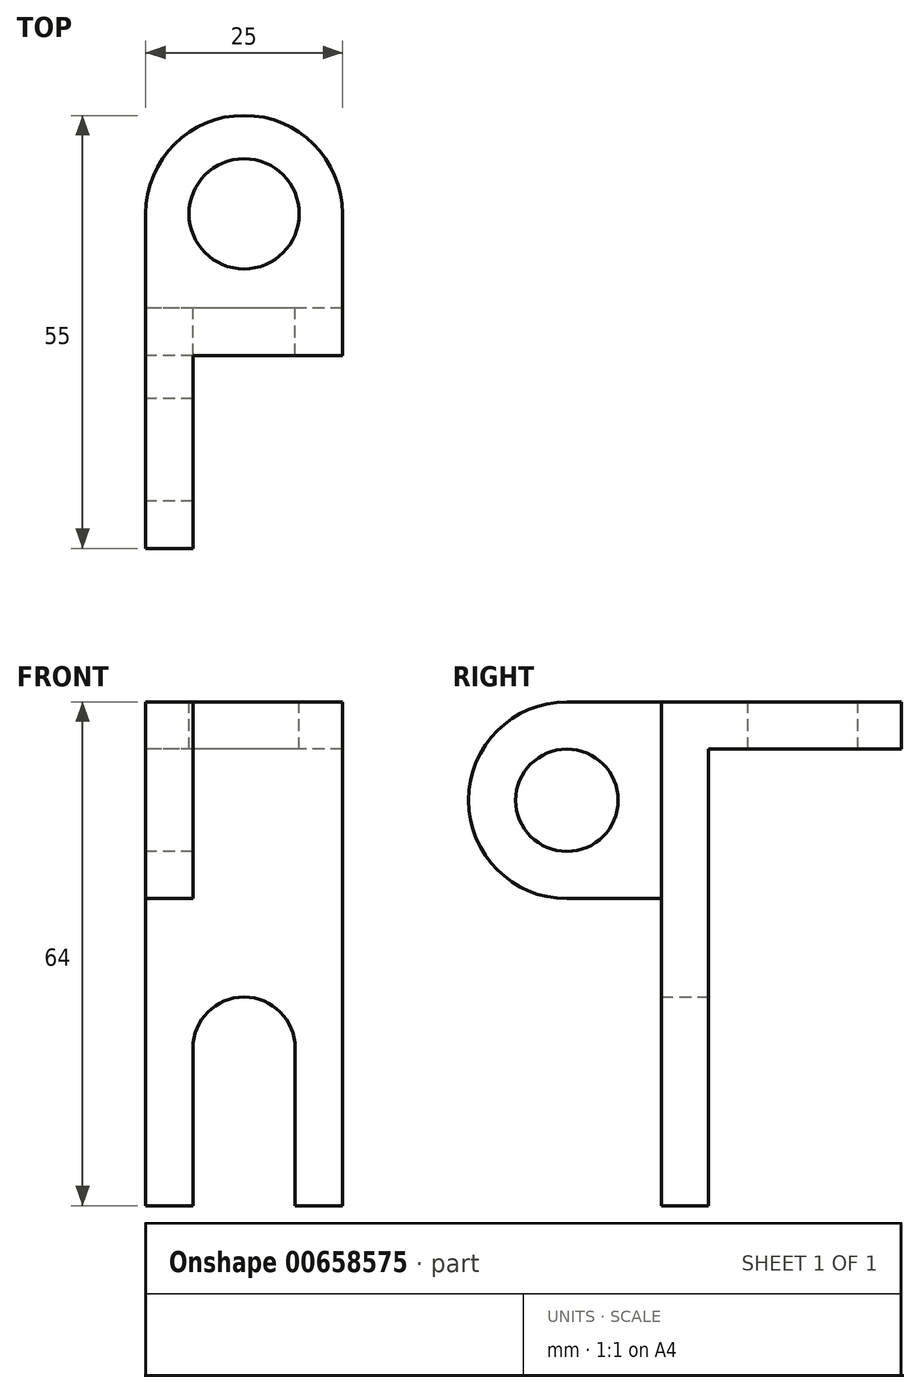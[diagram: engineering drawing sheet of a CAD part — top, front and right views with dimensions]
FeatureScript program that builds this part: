
annotation { "Feature Type Name" : "Feature", "Feature Type Description" : "" }
export const myFeature = defineFeature(function(context is Context, id is Id, definition is map)
    precondition{}
    {
        {
            var Q0;
            Q0=qCreatedBy(makeId("Front.planeOp"),FACE);
            var sketch = newSketch(context, id + "F0", { "sketchPlane" : qUnion([Q0])});
            skLineSegment(sketch, "E0.bottom", {"start": v(12.5, -32) * mm, "end": v(-12.5, -32) * mm});
            skLineSegment(sketch, "E0.top", {"start": v(12.5, 32) * mm, "end": v(-12.5, 32) * mm});
            skLineSegment(sketch, "E0.left", {"start": v(12.5, -32) * mm, "end": v(12.5, 32) * mm});
            skLineSegment(sketch, "E0.right", {"start": v(-12.5, -32) * mm, "end": v(-12.5, 32) * mm});
            skPoint(sketch, "E0.middle", {"position": v(0, 0) * mm});
            skLineSegment(sketch, "E1.bottom", {"start": v(-6.5, -32) * mm, "end": v(6.5, -32) * mm});
            skLineSegment(sketch, "E1.top", {"start": v(-6.5, -12) * mm, "end": v(6.5, -12) * mm});
            skLineSegment(sketch, "E1.left", {"start": v(-6.5, -32) * mm, "end": v(-6.5, -12) * mm});
            skLineSegment(sketch, "E1.right", {"start": v(6.5, -32) * mm, "end": v(6.5, -12) * mm});
            skPoint(sketch, "E1.middle", {"position": v(0, -22) * mm});
            skCircle(sketch, "E2", {"center": v(0, -12) * mm, "radius": 6.5 * mm});
            skSolve(sketch);
        }
        {
            var Q0;
            Q0=makeQuery(id+"F0.imprint","IMPRINT",FACE,{"disambiguationData":[TD([[makeQuery(id+"F0.imprint","IMPRINT",EDGE,{"derivedFrom":sQuery(id+"F0.wireOp",EDGE,"E0.bottom")}),-1.0]])]});
            extrude(context, id + "F1", {"entities" : qUnion([Q0]), "depth" : 6 * mm, "offsetDistance" : 25 * mm});
        }
        {
            var Q0;
            Q0=makeQuery(id+"F1.opExtrude","SWEPT_FACE",FACE,{"disambiguationData":[OSD([sQuery(id+"F0.wireOp",EDGE,"E0.top")])]});
            var sketch = newSketch(context, id + "F2", { "sketchPlane" : qUnion([Q0])});
            skLineSegment(sketch, "E3.bottom", {"start": v(12.5, -6) * mm, "end": v(-12.5, -6) * mm});
            skLineSegment(sketch, "E3.top", {"start": v(12.5, 12) * mm, "end": v(7, 12) * mm, "construction": true});
            skLineSegment(sketch, "E3.left", {"start": v(12.5, -6) * mm, "end": v(12.5, 12) * mm});
            skLineSegment(sketch, "E3.right", {"start": v(-12.5, -6) * mm, "end": v(-12.5, 12) * mm});
            skArc(sketch, "E4", {"start": v(12.5, 12) * mm, "mid": v(0, 24.5) * mm, "end": v(-12.5, 12) * mm});
            skCircle(sketch, "E5", {"center": v(0, 12) * mm, "radius": 7 * mm});
            skLineSegment(sketch, "E6.trimOffspring", {"start": v(-7, 12) * mm, "end": v(-12.5, 12) * mm, "construction": true});
            skSolve(sketch);
        }
        {
            var Q0;
            {var subQ0=sQuery(id+"F2.wireOp",EDGE,"E4");Q0=makeQuery(id+"F2.imprint","IMPRINT",FACE,{"disambiguationData":[TD([[makeQuery(id+"F2.imprint","IMPRINT",EDGE,{"derivedFrom":subQ0}),1.0]])]});}
            extrude(context, id + "F3", {"entities" : qUnion([Q0]), "operationType" : NewBodyOperationType.ADD, "oppositeDirection" : true, "depth" : 6 * mm, "offsetDistance" : 25 * mm});
        }
        {
            var Q0;
            Q0=makeQuery(id+"F3.boolean.opBoolean","MERGE",FACE,{"derivedFrom":[makeQuery(id+"F1.opExtrude","SWEPT_FACE",FACE,{"disambiguationData":[OSD([sQuery(id+"F0.wireOp",EDGE,"E0.right")])]}),makeQuery(id+"F3.opExtrude","SWEPT_FACE",FACE,{"disambiguationData":[OSD([sQuery(id+"F2.wireOp",EDGE,"E3.right")])]})]});
            var sketch = newSketch(context, id + "F4", { "sketchPlane" : qUnion([Q0])});
            skLineSegment(sketch, "E7.bottom", {"start": v(0, 32) * mm, "end": v(18, 32) * mm});
            skLineSegment(sketch, "E7.top", {"start": v(0, 7) * mm, "end": v(18, 7) * mm});
            skLineSegment(sketch, "E7.left", {"start": v(0, 32) * mm, "end": v(0, 7) * mm});
            skLineSegment(sketch, "E7.right", {"start": v(18, 32) * mm, "end": v(18, 7) * mm});
            skArc(sketch, "E8", {"start": v(18, 7) * mm, "mid": v(30.5, 19.5) * mm, "end": v(18, 32) * mm});
            skSolve(sketch);
        }
        {
            var Q0;
            {var subQ4=sQuery(id+"F4.wireOp",EDGE,"E7.right");Q0=makeQuery(id+"F4.imprint","IMPRINT",FACE,{"disambiguationData":[TD([[makeQuery(id+"F4.imprint","IMPRINT",EDGE,{"derivedFrom":subQ4}),-1.0]])]});}
            var Q1;
            Q1=makeQuery(id+"F4.imprint","IMPRINT",FACE,{"disambiguationData":[TD([[makeQuery(id+"F4.imprint","IMPRINT",EDGE,{"derivedFrom":sQuery(id+"F4.wireOp",EDGE,"E7.right")}),1.0]])]});
            extrude(context, id + "F5", {"entities" : qUnion([Q0, Q1]), "operationType" : NewBodyOperationType.ADD, "oppositeDirection" : true, "depth" : 6 * mm, "offsetDistance" : 25 * mm});
        }
        {
            var Q0;
            Q0=sQuery(id+"F4.wireOp",VERTEX,"E8.center");
            var Q1;
            Q1=makeQuery(id+"F1.opExtrude","SWEPT_BODY",BODY,{"disambiguationData":[OSD([sQuery(id+"F0.wireOp",EDGE,"E0.bottom"),sQuery(id+"F0.wireOp",EDGE,"E0.top"),sQuery(id+"F0.wireOp",EDGE,"E0.left"),sQuery(id+"F0.wireOp",EDGE,"E0.right"),sQuery(id+"F0.wireOp",EDGE,"E1.left"),sQuery(id+"F0.wireOp",EDGE,"E1.right"),sQuery(id+"F0.wireOp",EDGE,"E2")])]});
            hole(context, id + "F6", {"style" : HoleStyle.SIMPLE, "endStyle" : HoleEndStyle.THROUGH, "holeDiameter" : 13 * mm, "majorDiameter" : 5 * mm, "isTappedThrough" : true, "tappedDepth" : 12 * mm, "tapClearance" : 3, "locations" : qUnion([Q0]), "scope" : qUnion([Q1])});
        }
    });
